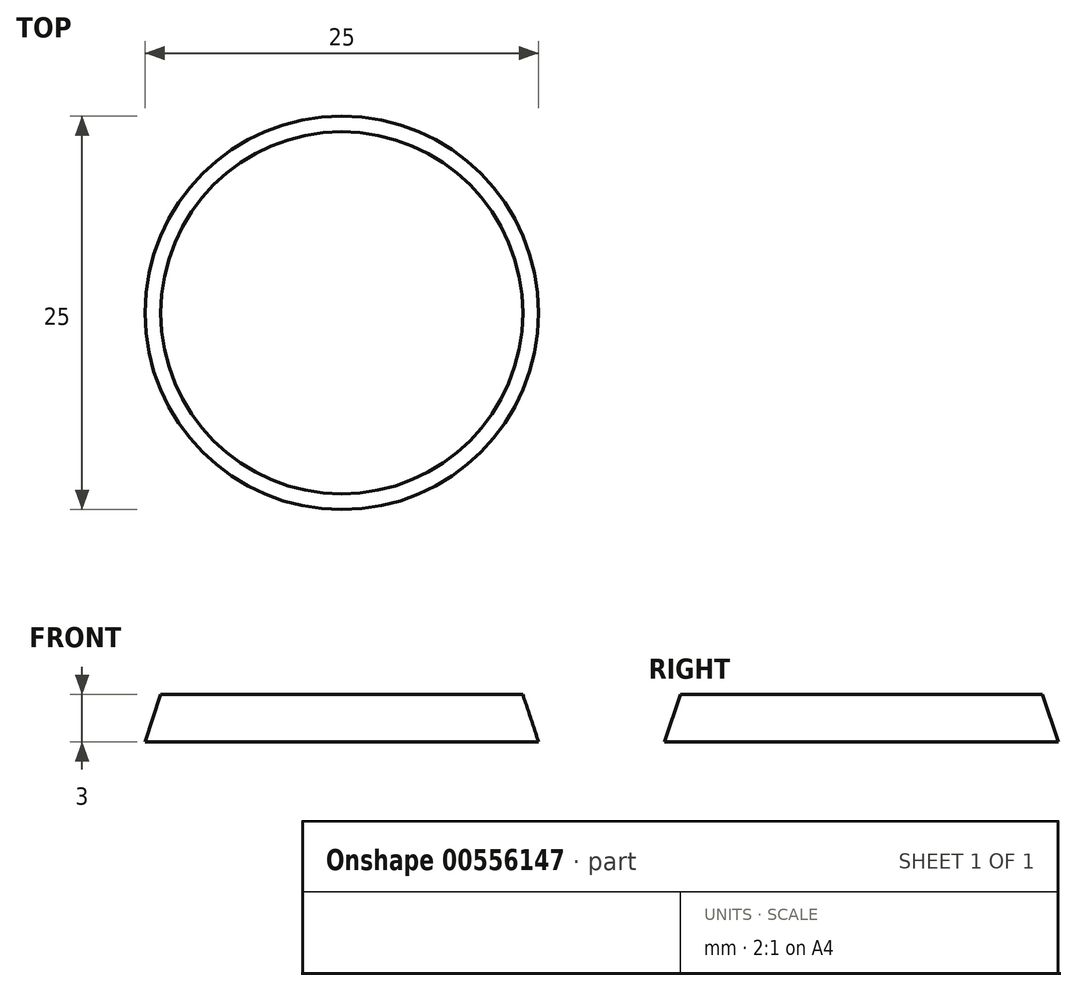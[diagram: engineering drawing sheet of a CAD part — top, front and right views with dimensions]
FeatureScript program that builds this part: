
annotation { "Feature Type Name" : "Feature", "Feature Type Description" : "" }
export const myFeature = defineFeature(function(context is Context, id is Id, definition is map)
    precondition{}
    {
        {
            var Q0;
            Q0=qCreatedBy(makeId("Top.planeOp"),FACE);
            var sketch = newSketch(context, id + "F0", { "sketchPlane" : qUnion([Q0])});
            skCircle(sketch, "E0", {"center": v(0, 0) * mm, "radius": 12.5 * mm});
            skSolve(sketch);
        }
        {
            var Q0;
            Q0=qCreatedBy(makeId("Top.planeOp"),FACE);
            cPlane(context, id + "F1", {"entities" : qUnion([Q0]), "cplaneType" : CPlaneType.OFFSET, "offset" : 3 * mm, "width" : 152.4 * mm, "height" : 152.4 * mm});
        }
        {
            var Q0;
            Q0=qCreatedBy(id+"F1.planeOp",FACE);
            var sketch = newSketch(context, id + "F2", { "sketchPlane" : qUnion([Q0])});
            skCircle(sketch, "E1", {"center": v(0, 0) * mm, "radius": 11.5 * mm});
            skSolve(sketch);
        }
        {
            var Q0;
            Q0=makeQuery(id+"F0.imprint","IMPRINT",FACE,{"disambiguationData":[TD([[makeQuery(id+"F0.imprint","IMPRINT",EDGE,{"derivedFrom":sQuery(id+"F0.wireOp",EDGE,"E0")}),1.0]])]});
            var Q1;
            Q1=makeQuery(id+"F2.imprint","IMPRINT",FACE,{"disambiguationData":[TD([[makeQuery(id+"F2.imprint","IMPRINT",EDGE,{"derivedFrom":sQuery(id+"F2.wireOp",EDGE,"E1")}),1.0]])]});
            loft(context, id + "F3", {"sheetProfilesArray" : [{ "sheetProfileEntities" : qUnion([Q0]) }, { "sheetProfileEntities" : qUnion([Q1]) }]});
        }
    });
